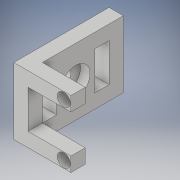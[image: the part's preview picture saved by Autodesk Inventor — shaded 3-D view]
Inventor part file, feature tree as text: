
AUTODESK INVENTOR PART (.ipt)
format: ipt  version: 2017 (Build 210142000, 142)  size: 178,688 bytes
history: native  units: in
note: dims shown in document units (in); Inventor stores cm internally (conversion verified against a paired STEP export)
features: extrude x5, sketch x4, projected_geometry x3
ambient origin geometry x8: Origin, YZ Plane, XZ Plane, XY Plane, X Axis, Y Axis, Z Axis, Center Point
bodies: Solid1 (feature_tree)
feature tree (12):
  sketch  "Sketch1"  dims[d8=0.5in d9=0.1875in]
  extrude  "Extrusion1"  Depth=0.1875in
  extrude  "Extrusion2"  Depth=0.1875in
  extrude  "Extrusion3"  Depth=0.375in
  extrude  "Extrusion4"  Depth=0.125in TaperAngle=0.0deg
  extrude  "Extrusion5"  Depth=0.75in
  sketch  "Sketch2"  dims[d10=0.1875in d11=0.1875in]
  projected_geometry  "Projected Loop1"
  sketch  "Sketch3"  dims[d12=0.1875in d13=0.0in d14=0.375in]
  sketch  "Sketch4"  dims[d15=0.4375in d17=0.125in d18=0.0in d21=0.75in d22=0.17in d23=0.0938in d24=0.17in d25=0.1875in d26=0.0in d28=0.1875in d29=0.1875in d31=0.247in d32=0.1235in d33=0.75in d34=0.0938in d35=0.0938in d37=1.25in d38=1.25in d39=0.875in d40=0.125in d41=1.0in d42=0.0in d43=0.1875in d44=0.0in d45=0.1875in d46=0.0938in d47=0.0in d48=0.5in d49=0.1875in d50=1.0in d51=0.0in d52=1.25in d53=0.625in]
  projected_geometry  "Projected Loop4"
  projected_geometry  "Projected Loop5"
